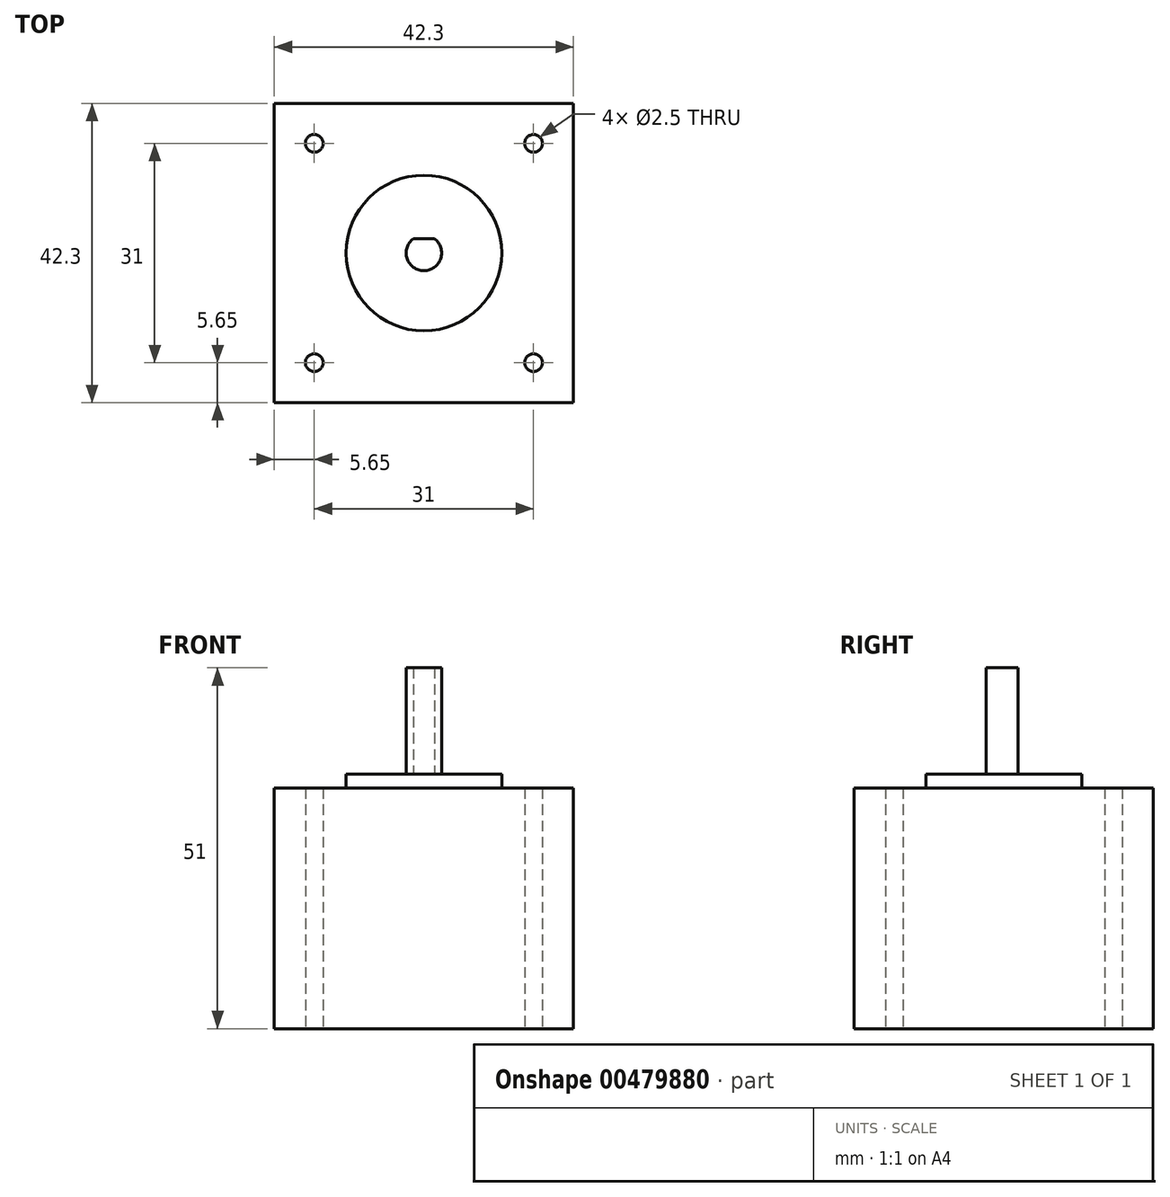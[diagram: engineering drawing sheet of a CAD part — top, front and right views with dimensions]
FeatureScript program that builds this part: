
annotation { "Feature Type Name" : "Feature", "Feature Type Description" : "" }
export const myFeature = defineFeature(function(context is Context, id is Id, definition is map)
    precondition{}
    {
        {
            var Q0;
            Q0=qCreatedBy(makeId("Top.planeOp"),FACE);
            var sketch = newSketch(context, id + "F0", { "sketchPlane" : qUnion([Q0])});
            skLineSegment(sketch, "E0.bottom", {"start": v(0, 0) * mm, "end": v(42.3, 0) * mm});
            skLineSegment(sketch, "E0.top", {"start": v(0, 42.3) * mm, "end": v(42.3, 42.3) * mm});
            skLineSegment(sketch, "E0.left", {"start": v(0, 0) * mm, "end": v(0, 42.3) * mm});
            skLineSegment(sketch, "E0.right", {"start": v(42.3, 0) * mm, "end": v(42.3, 42.3) * mm});
            skCircle(sketch, "E1", {"center": v(21.15, 21.15) * mm, "radius": 11 * mm});
            skPoint(sketch, "E1.centerSnap0", {"position": v(0, 21.15) * mm});
            skPoint(sketch, "E1.centerSnap1", {"position": v(21.15, 42.3) * mm});
            skCircle(sketch, "E2", {"center": v(5.65, 36.65) * mm, "radius": 1.25 * mm});
            skCircle(sketch, "E3.1.0", {"center": v(5.65, 5.65) * mm, "radius": 1.25 * mm});
            skCircle(sketch, "E3.2.0", {"center": v(36.65, 5.65) * mm, "radius": 1.25 * mm});
            skCircle(sketch, "E3.3.0", {"center": v(36.65, 36.65) * mm, "radius": 1.25 * mm});
            skSolve(sketch);
        }
        {
            var Q0;
            Q0=makeQuery(id+"F0.imprint","IMPRINT",FACE,{"disambiguationData":[TD([[makeQuery(id+"F0.imprint","IMPRINT",EDGE,{"derivedFrom":sQuery(id+"F0.wireOp",EDGE,"E0.bottom")}),1.0]])]});
            var Q1;
            Q1=makeQuery(id+"F0.imprint","IMPRINT",FACE,{"disambiguationData":[TD([[makeQuery(id+"F0.imprint","IMPRINT",EDGE,{"derivedFrom":sQuery(id+"F0.wireOp",EDGE,"E1")}),1.0]])]});
            extrude(context, id + "F1", {"entities" : qUnion([Q0, Q1]), "depth" : 34 * mm});
        }
        {
            var Q0;
            Q0=makeQuery(id+"F0.imprint","IMPRINT",FACE,{"disambiguationData":[TD([[makeQuery(id+"F0.imprint","IMPRINT",EDGE,{"derivedFrom":sQuery(id+"F0.wireOp",EDGE,"E1")}),1.0]])]});
            var Q1;
            Q1=makeQuery(id+"F1.opExtrude","CAP_FACE",FACE,{"disambiguationData":[OSD([sQuery(id+"F0.wireOp",EDGE,"E0.bottom"),sQuery(id+"F0.wireOp",EDGE,"E0.top"),sQuery(id+"F0.wireOp",EDGE,"E0.left"),sQuery(id+"F0.wireOp",EDGE,"E0.right"),sQuery(id+"F0.wireOp",EDGE,"E2"),sQuery(id+"F0.wireOp",EDGE,"E3.1.0"),sQuery(id+"F0.wireOp",EDGE,"E3.2.0"),sQuery(id+"F0.wireOp",EDGE,"E3.3.0")])],"isStart":false});
            extrude(context, id + "F2", {"entities" : qUnion([Q0]), "operationType" : NewBodyOperationType.ADD, "depth" : 36 * mm});
        }
        {
            var Q0;
            Q0=makeQuery(id+"F2.opExtrude","CAP_FACE",FACE,{"disambiguationData":[OSD([sQuery(id+"F0.wireOp",EDGE,"E1")])],"isStart":false});
            var sketch = newSketch(context, id + "F3", { "sketchPlane" : qUnion([Q0])});
            skArc(sketch, "E4", {"start": v(19.65, 23.15) * mm, "mid": v(21.15, 18.65) * mm, "end": v(22.65, 23.15) * mm});
            skLineSegment(sketch, "E5", {"start": v(19.65, 23.15) * mm, "end": v(22.65, 23.15) * mm});
            skSolve(sketch);
        }
        {
            var Q0;
            Q0 = qSketchRegion(id + "F3", true);
            extrude(context, id + "F4", {"entities" : qUnion([Q0]), "operationType" : NewBodyOperationType.ADD, "depth" : 15 * mm});
        }
    });
